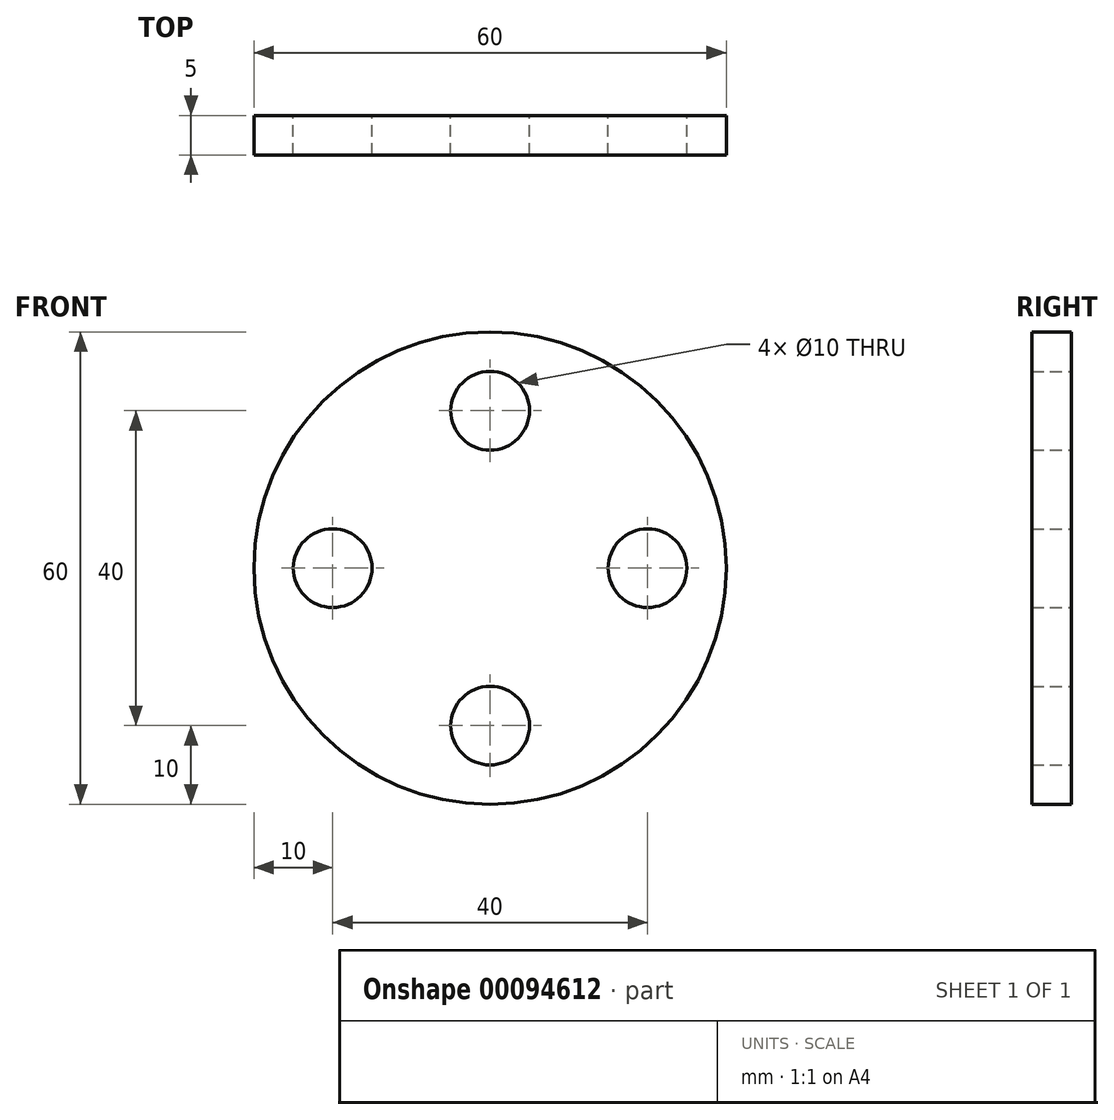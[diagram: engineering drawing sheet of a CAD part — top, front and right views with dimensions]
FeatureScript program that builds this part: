
annotation { "Feature Type Name" : "Feature", "Feature Type Description" : "" }
export const myFeature = defineFeature(function(context is Context, id is Id, definition is map)
    precondition{}
    {
        {
            var Q0;
            Q0=qCreatedBy(makeId("Front.planeOp"),FACE);
            var sketch = newSketch(context, id + "F0", { "sketchPlane" : qUnion([Q0])});
            skCircle(sketch, "E0", {"center": v(0, 0) * mm, "radius": 30 * mm});
            skCircle(sketch, "E1", {"center": v(0, 0) * mm, "radius": 20 * mm, "construction": true});
            skLineSegment(sketch, "E2", {"start": v(-53.01, 0) * mm, "end": v(54.36, 0) * mm, "construction": true});
            skLineSegment(sketch, "E3", {"start": v(0, 46.94) * mm, "end": v(0, -48.68) * mm, "construction": true});
            skCircle(sketch, "E4", {"center": v(-20, 0) * mm, "radius": 5 * mm});
            skCircle(sketch, "E5", {"center": v(20, 0) * mm, "radius": 5 * mm});
            skCircle(sketch, "E6", {"center": v(0, 20) * mm, "radius": 5 * mm});
            skCircle(sketch, "E7", {"center": v(0, -20) * mm, "radius": 5 * mm});
            skSolve(sketch);
        }
        {
            var Q0;
            Q0 = qSketchRegion(id + "F0", true);
            extrude(context, id + "F1", {"entities" : qUnion([Q0]), "depth" : 5 * mm});
        }
    });
